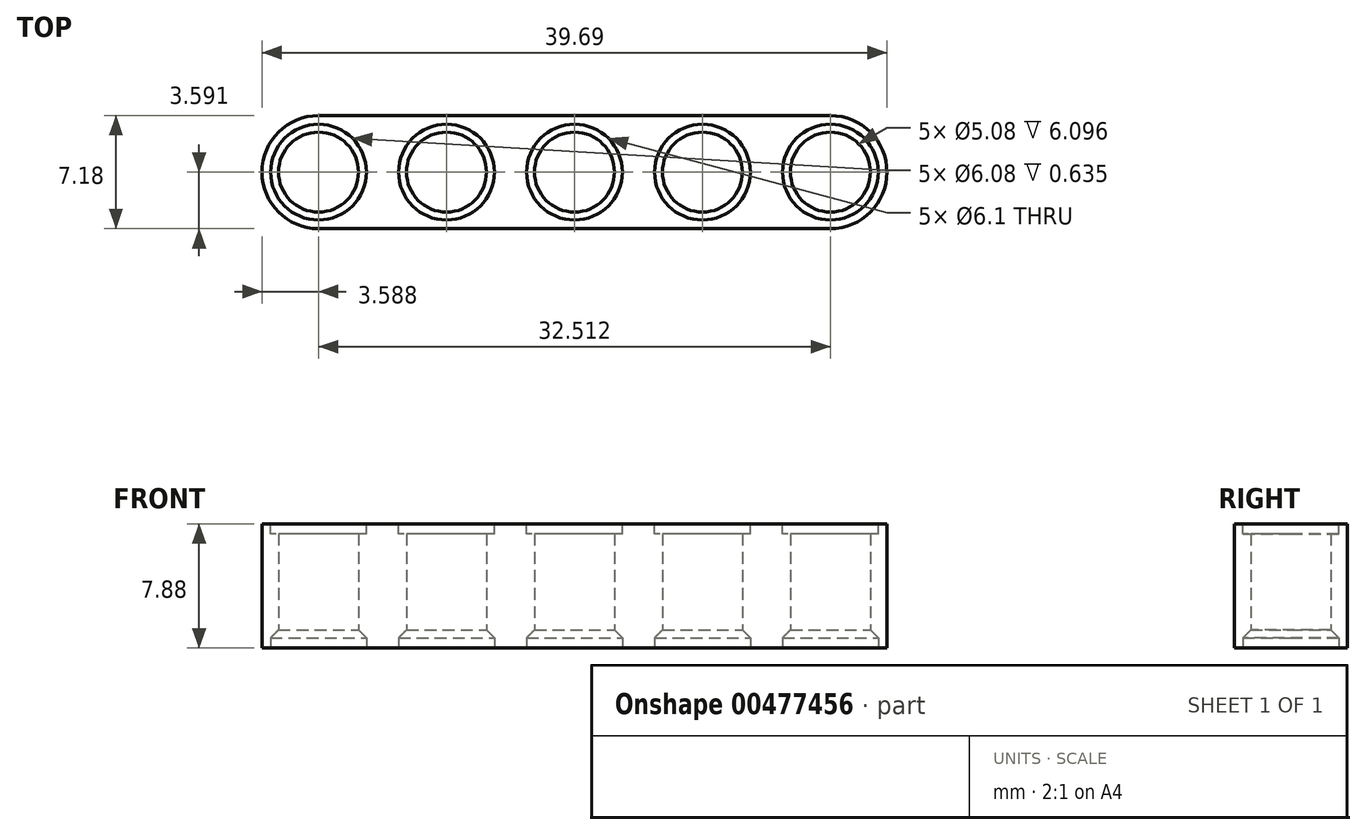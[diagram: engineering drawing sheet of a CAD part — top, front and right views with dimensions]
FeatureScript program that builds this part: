
annotation { "Feature Type Name" : "Feature", "Feature Type Description" : "" }
export const myFeature = defineFeature(function(context is Context, id is Id, definition is map)
    precondition{}
    {
        {
            var Q0;
            Q0=qCreatedBy(makeId("Top.planeOp"),FACE);
            var sketch = newSketch(context, id + "F0", { "sketchPlane" : qUnion([Q0])});
            skCircle(sketch, "E0", {"center": v(-60.84, 14.37) * mm, "radius": 3.6 * mm});
            skCircle(sketch, "E1.1.0.0", {"center": v(-52.71, 14.37) * mm, "radius": 3.6 * mm});
            skCircle(sketch, "E1.2.0.0", {"center": v(-44.59, 14.37) * mm, "radius": 3.6 * mm});
            skCircle(sketch, "E1.3.0.0", {"center": v(-36.46, 14.37) * mm, "radius": 3.6 * mm});
            skLineSegment(sketch, "E1.direction1", {"start": v(-60.84, 14.37) * mm, "end": v(-52.71, 14.37) * mm, "construction": true});
            skCircle(sketch, "E2.0.4.0", {"center": v(-28.33, 14.37) * mm, "radius": 3.6 * mm});
            skLineSegment(sketch, "E3.left", {"start": v(-60.84, 14.37) * mm, "end": v(-60.84, 14.37) * mm});
            skLineSegment(sketch, "E3.right", {"start": v(-28.33, 14.37) * mm, "end": v(-28.33, 14.37) * mm});
            skLineSegment(sketch, "E4.bottom", {"start": v(-60.84, 17.96) * mm, "end": v(-28.33, 17.96) * mm});
            skLineSegment(sketch, "E4.top", {"start": v(-60.84, 10.78) * mm, "end": v(-28.33, 10.78) * mm});
            skCircle(sketch, "E5", {"center": v(-60.84, 14.37) * mm, "radius": 3.05 * mm});
            skCircle(sketch, "E6.1.0.0", {"center": v(-52.71, 14.37) * mm, "radius": 3.05 * mm});
            skCircle(sketch, "E6.2.0.0", {"center": v(-44.59, 14.37) * mm, "radius": 3.05 * mm});
            skCircle(sketch, "E6.3.0.0", {"center": v(-36.46, 14.37) * mm, "radius": 3.05 * mm});
            skCircle(sketch, "E6.4.0.0", {"center": v(-28.33, 14.37) * mm, "radius": 3.05 * mm});
            skCircle(sketch, "E7", {"center": v(-60.84, 14.37) * mm, "radius": 2.54 * mm});
            skCircle(sketch, "E8.1.0.0", {"center": v(-52.71, 14.37) * mm, "radius": 2.54 * mm});
            skCircle(sketch, "E8.2.0.0", {"center": v(-44.59, 14.37) * mm, "radius": 2.54 * mm});
            skCircle(sketch, "E8.3.0.0", {"center": v(-36.46, 14.37) * mm, "radius": 2.54 * mm});
            skCircle(sketch, "E8.4.0.0", {"center": v(-28.33, 14.37) * mm, "radius": 2.54 * mm});
            skSolve(sketch);
        }
        {
            var Q0;
            Q0=makeQuery(id+"F0.imprint","IMPRINT",FACE,{"disambiguationData":[TD([[makeQuery(id+"F0.imprint","IMPRINT",EDGE,{"derivedFrom":sQuery(id+"F0.wireOp",EDGE,"E6.2.0.0")}),1.0]])]});
            var Q1;
            {var subQ0=sQuery(id+"F0.wireOp",EDGE,"E4.bottom");var subQ1=sQuery(id+"F0.wireOp",EDGE,"E0");var subQ2=makeQuery(id+"F0.imprint","INTERSECT",VERTEX,{"derivedFrom":[subQ1,subQ0]});Q1=makeQuery(id+"F0.imprint","IMPRINT",FACE,{"disambiguationData":[TD([[makeQuery(id+"F0.imprint","IMPRINT",EDGE,{"disambiguationData":[TD([[subQ2,1.0]])],"derivedFrom":subQ1}),-1.0]])]});}
            var Q2;
            {var subQ0=sQuery(id+"F0.wireOp",EDGE,"E4.bottom");var subQ1=sQuery(id+"F0.wireOp",EDGE,"E1.1.0.0");var subQ2=makeQuery(id+"F0.imprint","INTERSECT",VERTEX,{"derivedFrom":[subQ1,subQ0]});Q2=makeQuery(id+"F0.imprint","IMPRINT",FACE,{"disambiguationData":[TD([[makeQuery(id+"F0.imprint","IMPRINT",EDGE,{"disambiguationData":[TD([[subQ2,1.0]])],"derivedFrom":subQ1}),-1.0]])]});}
            var Q3;
            Q3=makeQuery(id+"F0.imprint","IMPRINT",FACE,{"disambiguationData":[TD([[makeQuery(id+"F0.imprint","IMPRINT",EDGE,{"derivedFrom":sQuery(id+"F0.wireOp",EDGE,"E6.2.0.0")}),-1.0]])]});
            var Q4;
            Q4=makeQuery(id+"F0.imprint","IMPRINT",FACE,{"disambiguationData":[TD([[makeQuery(id+"F0.imprint","IMPRINT",EDGE,{"derivedFrom":sQuery(id+"F0.wireOp",EDGE,"E6.1.0.0")}),-1.0]])]});
            var Q5;
            Q5=makeQuery(id+"F0.imprint","IMPRINT",FACE,{"disambiguationData":[TD([[makeQuery(id+"F0.imprint","IMPRINT",EDGE,{"derivedFrom":sQuery(id+"F0.wireOp",EDGE,"E6.3.0.0")}),-1.0]])]});
            var Q6;
            Q6=makeQuery(id+"F0.imprint","IMPRINT",FACE,{"disambiguationData":[TD([[makeQuery(id+"F0.imprint","IMPRINT",EDGE,{"derivedFrom":sQuery(id+"F0.wireOp",EDGE,"E6.3.0.0")}),1.0]])]});
            var Q7;
            {var subQ0=sQuery(id+"F0.wireOp",EDGE,"E4.bottom");var subQ1=sQuery(id+"F0.wireOp",EDGE,"E1.3.0.0");var subQ2=makeQuery(id+"F0.imprint","INTERSECT",VERTEX,{"derivedFrom":[subQ1,subQ0]});Q7=makeQuery(id+"F0.imprint","IMPRINT",FACE,{"disambiguationData":[TD([[makeQuery(id+"F0.imprint","IMPRINT",EDGE,{"disambiguationData":[TD([[subQ2,1.0]])],"derivedFrom":subQ1}),-1.0]])]});}
            var Q8;
            Q8=makeQuery(id+"F0.imprint","IMPRINT",FACE,{"disambiguationData":[TD([[makeQuery(id+"F0.imprint","IMPRINT",EDGE,{"derivedFrom":sQuery(id+"F0.wireOp",EDGE,"E6.4.0.0")}),-1.0]])]});
            var Q9;
            Q9=makeQuery(id+"F0.imprint","IMPRINT",FACE,{"disambiguationData":[TD([[makeQuery(id+"F0.imprint","IMPRINT",EDGE,{"derivedFrom":sQuery(id+"F0.wireOp",EDGE,"E6.1.0.0")}),1.0]])]});
            var Q10;
            {var subQ0=sQuery(id+"F0.wireOp",EDGE,"E4.bottom");var subQ1=sQuery(id+"F0.wireOp",EDGE,"E1.2.0.0");var subQ2=makeQuery(id+"F0.imprint","INTERSECT",VERTEX,{"derivedFrom":[subQ1,subQ0]});Q10=makeQuery(id+"F0.imprint","IMPRINT",FACE,{"disambiguationData":[TD([[makeQuery(id+"F0.imprint","IMPRINT",EDGE,{"disambiguationData":[TD([[subQ2,1.0]])],"derivedFrom":subQ1}),-1.0]])]});}
            var Q11;
            Q11=makeQuery(id+"F0.imprint","IMPRINT",FACE,{"disambiguationData":[TD([[makeQuery(id+"F0.imprint","IMPRINT",EDGE,{"derivedFrom":sQuery(id+"F0.wireOp",EDGE,"E6.4.0.0")}),1.0]])]});
            var Q12;
            Q12=makeQuery(id+"F0.imprint","IMPRINT",FACE,{"disambiguationData":[TD([[makeQuery(id+"F0.imprint","IMPRINT",EDGE,{"derivedFrom":sQuery(id+"F0.wireOp",EDGE,"E5")}),-1.0]])]});
            var Q13;
            Q13=makeQuery(id+"F0.imprint","IMPRINT",FACE,{"disambiguationData":[TD([[makeQuery(id+"F0.imprint","IMPRINT",EDGE,{"derivedFrom":sQuery(id+"F0.wireOp",EDGE,"E5")}),1.0]])]});
            extrude(context, id + "F1", {"entities" : qUnion([Q0, Q1, Q2, Q3, Q4, Q5, Q6, Q7, Q8, Q9, Q10, Q11, Q12, Q13]), "endBound" : BoundingType.SYMMETRIC, "depth" : 7.87 * mm});
        }
        {
            var Q0;
            Q0=makeQuery(id+"F1.opExtrude","CAP_FACE",FACE,{"disambiguationData":[OSD([sQuery(id+"F0.wireOp",EDGE,"E0"),sQuery(id+"F0.wireOp",EDGE,"E2.0.4.0"),sQuery(id+"F0.wireOp",EDGE,"E4.bottom"),sQuery(id+"F0.wireOp",EDGE,"E4.top"),sQuery(id+"F0.wireOp",EDGE,"E7"),sQuery(id+"F0.wireOp",EDGE,"E8.1.0.0"),sQuery(id+"F0.wireOp",EDGE,"E8.2.0.0"),sQuery(id+"F0.wireOp",EDGE,"E8.3.0.0"),sQuery(id+"F0.wireOp",EDGE,"E8.4.0.0")])],"isStart":false});
            var sketch = newSketch(context, id + "F2", { "sketchPlane" : qUnion([Q0])});
            skCircle(sketch, "E9", {"center": v(-28.33, 14.37) * mm, "radius": 3.04 * mm});
            skCircle(sketch, "E10.1.0.0", {"center": v(-36.46, 14.37) * mm, "radius": 3.04 * mm});
            skCircle(sketch, "E10.2.0.0", {"center": v(-44.59, 14.37) * mm, "radius": 3.04 * mm});
            skCircle(sketch, "E10.3.0.0", {"center": v(-52.71, 14.37) * mm, "radius": 3.04 * mm});
            skCircle(sketch, "E10.4.0.0", {"center": v(-60.84, 14.37) * mm, "radius": 3.04 * mm});
            skLineSegment(sketch, "E10.direction1", {"start": v(-28.33, 14.37) * mm, "end": v(-36.46, 14.37) * mm, "construction": true});
            skSolve(sketch);
        }
        {
            var Q0;
            Q0=qSketchRegion(id+"F2",true);
            extrude(context, id + "F3", {"entities" : qUnion([Q0]), "operationType" : NewBodyOperationType.REMOVE, "oppositeDirection" : true, "depth" : 0.64 * mm});
        }
        {
            var Q0;
            Q0=makeQuery(id+"F1.opExtrude","CAP_FACE",FACE,{"disambiguationData":[OSD([sQuery(id+"F0.wireOp",EDGE,"E0"),sQuery(id+"F0.wireOp",EDGE,"E2.0.4.0"),sQuery(id+"F0.wireOp",EDGE,"E4.bottom"),sQuery(id+"F0.wireOp",EDGE,"E4.top"),sQuery(id+"F0.wireOp",EDGE,"E7"),sQuery(id+"F0.wireOp",EDGE,"E8.1.0.0"),sQuery(id+"F0.wireOp",EDGE,"E8.2.0.0"),sQuery(id+"F0.wireOp",EDGE,"E8.3.0.0"),sQuery(id+"F0.wireOp",EDGE,"E8.4.0.0")])],"isStart":true});
            var sketch = newSketch(context, id + "F4", { "sketchPlane" : qUnion([Q0])});
            skCircle(sketch, "E11", {"center": v(-60.84, -14.37) * mm, "radius": 3.05 * mm});
            skCircle(sketch, "E12.1.0.0", {"center": v(-52.71, -14.37) * mm, "radius": 3.05 * mm});
            skCircle(sketch, "E12.2.0.0", {"center": v(-44.59, -14.37) * mm, "radius": 3.05 * mm});
            skCircle(sketch, "E12.3.0.0", {"center": v(-36.46, -14.37) * mm, "radius": 3.05 * mm});
            skCircle(sketch, "E12.4.0.0", {"center": v(-28.33, -14.37) * mm, "radius": 3.05 * mm});
            skLineSegment(sketch, "E12.direction1", {"start": v(-60.84, -14.37) * mm, "end": v(-52.71, -14.37) * mm, "construction": true});
            skSolve(sketch);
        }
        {
            var Q0;
            Q0=qSketchRegion(id+"F4",true);
            extrude(context, id + "F5", {"entities" : qUnion([Q0]), "operationType" : NewBodyOperationType.REMOVE, "oppositeDirection" : true, "depth" : 0.64 * mm});
        }
        {
            var Q0;
            Q0=makeQuery(id+"F5.boolean.opBoolean","INTERSECT",EDGE,{"derivedFrom":[makeQuery(id+"F1.opExtrude","SWEPT_FACE",FACE,{"disambiguationData":[OSD([sQuery(id+"F0.wireOp",EDGE,"E8.3.0.0")])]}),makeQuery(id+"F5.opExtrude","CAP_FACE",FACE,{"disambiguationData":[OSD([sQuery(id+"F4.wireOp",EDGE,"E12.3.0.0")])],"isStart":false})]});
            chamfer(context, id + "F6", {"entities" : qUnion([Q0]), "chamferType" : ChamferType.OFFSET_ANGLE, "width" : 0.5 * mm, "oppositeDirection" : false, "angle" : 45 * degree});
        }
        {
            var Q0;
            Q0=makeQuery(id+"F5.boolean.opBoolean","INTERSECT",EDGE,{"derivedFrom":[makeQuery(id+"F1.opExtrude","SWEPT_FACE",FACE,{"disambiguationData":[OSD([sQuery(id+"F0.wireOp",EDGE,"E8.2.0.0")])]}),makeQuery(id+"F5.opExtrude","CAP_FACE",FACE,{"disambiguationData":[OSD([sQuery(id+"F4.wireOp",EDGE,"E12.2.0.0")])],"isStart":false})]});
            var Q1;
            Q1=makeQuery(id+"F5.boolean.opBoolean","INTERSECT",EDGE,{"derivedFrom":[makeQuery(id+"F1.opExtrude","SWEPT_FACE",FACE,{"disambiguationData":[OSD([sQuery(id+"F0.wireOp",EDGE,"E8.1.0.0")])]}),makeQuery(id+"F5.opExtrude","CAP_FACE",FACE,{"disambiguationData":[OSD([sQuery(id+"F4.wireOp",EDGE,"E12.1.0.0")])],"isStart":false})]});
            var Q2;
            Q2=makeQuery(id+"F5.boolean.opBoolean","INTERSECT",EDGE,{"derivedFrom":[makeQuery(id+"F1.opExtrude","SWEPT_FACE",FACE,{"disambiguationData":[OSD([sQuery(id+"F0.wireOp",EDGE,"E7")])]}),makeQuery(id+"F5.opExtrude","CAP_FACE",FACE,{"disambiguationData":[OSD([sQuery(id+"F4.wireOp",EDGE,"E11")])],"isStart":false})]});
            var Q3;
            Q3=makeQuery(id+"F5.boolean.opBoolean","INTERSECT",EDGE,{"derivedFrom":[makeQuery(id+"F1.opExtrude","SWEPT_FACE",FACE,{"disambiguationData":[OSD([sQuery(id+"F0.wireOp",EDGE,"E8.4.0.0")])]}),makeQuery(id+"F5.opExtrude","CAP_FACE",FACE,{"disambiguationData":[OSD([sQuery(id+"F4.wireOp",EDGE,"E12.4.0.0")])],"isStart":false})]});
            chamfer(context, id + "F7", {"entities" : qUnion([Q0, Q1, Q2, Q3]), "chamferType" : ChamferType.OFFSET_ANGLE, "width" : 0.5 * mm, "oppositeDirection" : false, "angle" : 45 * degree});
        }
    });
